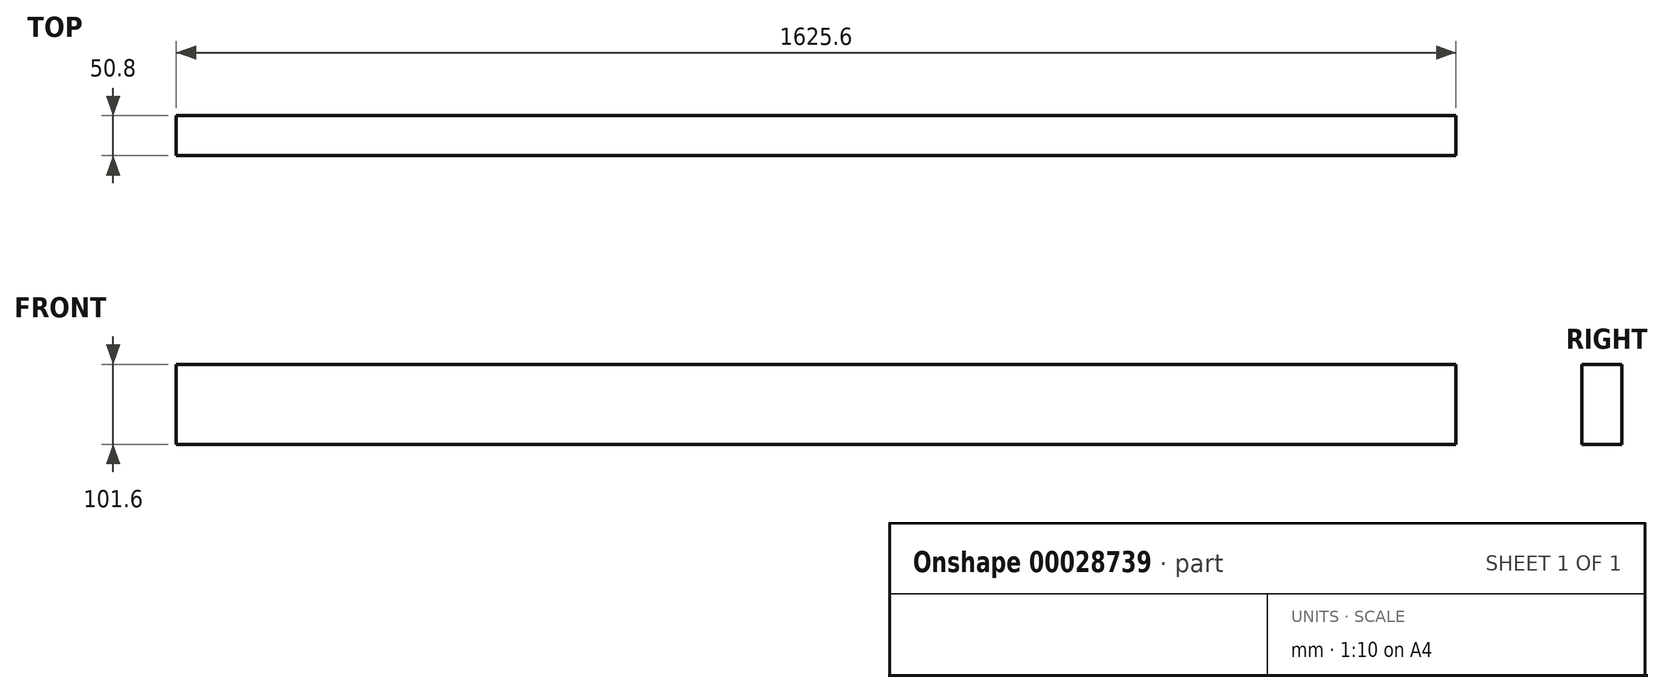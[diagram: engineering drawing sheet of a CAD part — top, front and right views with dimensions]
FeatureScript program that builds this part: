
annotation { "Feature Type Name" : "Feature", "Feature Type Description" : "" }
export const myFeature = defineFeature(function(context is Context, id is Id, definition is map)
    precondition{}
    {
        {
            var Q0;
            Q0=qCreatedBy(makeId("Right.planeOp"),FACE);
            var sketch = newSketch(context, id + "F0", { "sketchPlane" : qUnion([Q0])});
            skLineSegment(sketch, "E0.bottom", {"start": v(-32.94, 50.8) * mm, "end": v(17.86, 50.8) * mm});
            skLineSegment(sketch, "E0.top", {"start": v(-32.94, -50.8) * mm, "end": v(17.86, -50.8) * mm});
            skLineSegment(sketch, "E0.left", {"start": v(-32.94, 50.8) * mm, "end": v(-32.94, -50.8) * mm});
            skLineSegment(sketch, "E0.right", {"start": v(17.86, 50.8) * mm, "end": v(17.86, -50.8) * mm});
            skSolve(sketch);
        }
        {
            var Q0;
            Q0=makeQuery(id+"F0.imprint","IMPRINT",FACE,{"disambiguationData":[TD([[makeQuery(id+"F0.imprint","IMPRINT",EDGE,{"derivedFrom":sQuery(id+"F0.wireOp",EDGE,"E0.bottom")}),-1.0]])]});
            extrude(context, id + "F1", {"entities" : qUnion([Q0]), "endBound" : BoundingType.SYMMETRIC, "depth" : 1625.6 * mm});
        }
    });
